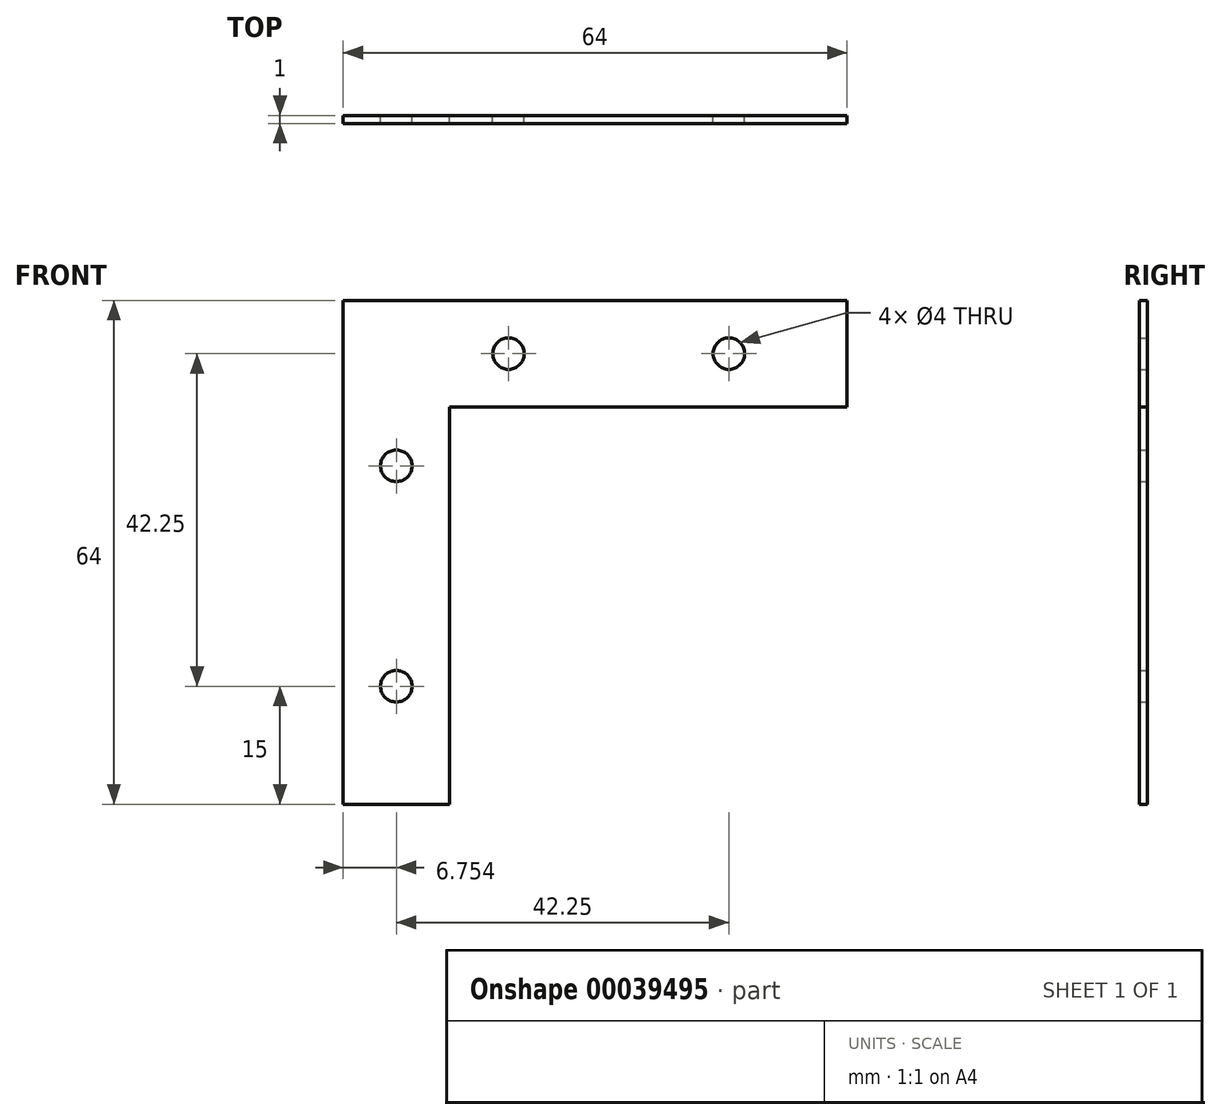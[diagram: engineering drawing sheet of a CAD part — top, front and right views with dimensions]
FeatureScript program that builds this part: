
annotation { "Feature Type Name" : "Feature", "Feature Type Description" : "" }
export const myFeature = defineFeature(function(context is Context, id is Id, definition is map)
    precondition{}
    {
        {
            var Q0;
            Q0=qCreatedBy(makeId("Front.planeOp"),FACE);
            var sketch = newSketch(context, id + "F0", { "sketchPlane" : qUnion([Q0])});
            skLineSegment(sketch, "E0", {"start": v(-37.97, -30.87) * mm, "end": v(-37.97, 33.13) * mm});
            skLineSegment(sketch, "E1", {"start": v(-37.97, 33.13) * mm, "end": v(26.03, 33.13) * mm});
            skLineSegment(sketch, "E2", {"start": v(26.03, 33.13) * mm, "end": v(26.03, 19.63) * mm});
            skLineSegment(sketch, "E3", {"start": v(26.03, 19.63) * mm, "end": v(-24.47, 19.63) * mm});
            skLineSegment(sketch, "E4", {"start": v(-24.47, 19.63) * mm, "end": v(-24.47, -30.87) * mm});
            skLineSegment(sketch, "E5", {"start": v(-24.47, -30.87) * mm, "end": v(-37.97, -30.87) * mm});
            skLineSegment(sketch, "E6", {"start": v(11.03, 33.13) * mm, "end": v(11.03, 19.63) * mm, "construction": true});
            skCircle(sketch, "E7", {"center": v(11.03, 26.38) * mm, "radius": 2 * mm});
            skCircle(sketch, "E8", {"center": v(-16.97, 26.38) * mm, "radius": 2 * mm});
            skCircle(sketch, "E9", {"center": v(-31.22, -15.87) * mm, "radius": 2 * mm});
            skLineSegment(sketch, "E10", {"start": v(-37.97, -15.87) * mm, "end": v(-24.47, -15.87) * mm, "construction": true});
            skCircle(sketch, "E11", {"center": v(-31.22, 12.13) * mm, "radius": 2 * mm});
            skSolve(sketch);
        }
        {
            var Q0;
            Q0=qSketchRegion(id+"F0",true);
            extrude(context, id + "F1", {"entities" : qUnion([Q0]), "endBound" : BoundingType.SYMMETRIC, "depth" : 1 * mm});
        }
    });
